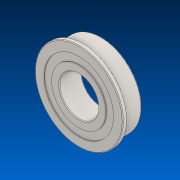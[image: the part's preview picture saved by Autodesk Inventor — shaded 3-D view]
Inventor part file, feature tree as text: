
AUTODESK INVENTOR PART (.ipt)
format: ipt  version: 2022.2 (Build 262287000, 287)  size: 200,192 bytes
history: native  units: in
note: dims shown in document units (in); Inventor stores cm internally (conversion verified against a paired STEP export)
features: fillet x1
ambient origin geometry x8: Origin, YZ Plane, XZ Plane, XY Plane, X Axis, Y Axis, Z Axis, Center Point
bodies: Solid1 (feature_tree)
feature tree (1):
  fillet  "Fillet1"  [1 undecoded]
note: 1 required parameter value undecoded (feature->parameter linkage not recoverable at this tier; creation-order binding heuristic only, values carry confidence <= 0.55)
